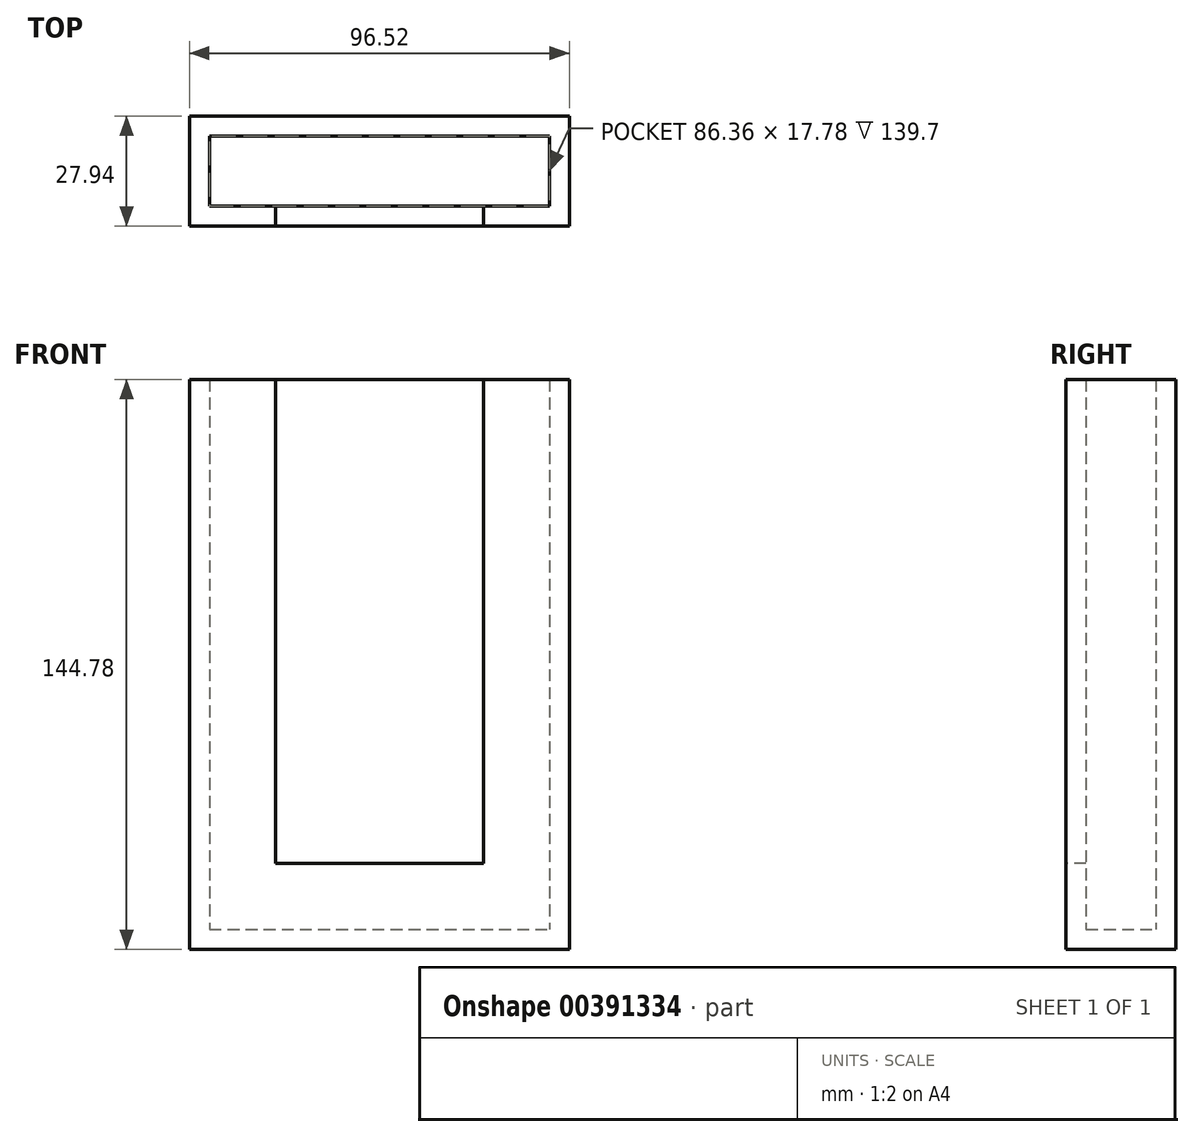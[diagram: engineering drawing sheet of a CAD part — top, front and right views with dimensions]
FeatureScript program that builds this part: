
annotation { "Feature Type Name" : "Feature", "Feature Type Description" : "" }
export const myFeature = defineFeature(function(context is Context, id is Id, definition is map)
    precondition{}
    {
        {
            var Q0;
            Q0=qCreatedBy(makeId("Front.planeOp"),FACE);
            var sketch = newSketch(context, id + "F0", { "sketchPlane" : qUnion([Q0])});
            skLineSegment(sketch, "E0.bottom", {"start": v(-60.88, 53.43) * mm, "end": v(35.64, 53.43) * mm});
            skLineSegment(sketch, "E0.top", {"start": v(-60.88, -91.35) * mm, "end": v(35.64, -91.35) * mm});
            skLineSegment(sketch, "E0.left", {"start": v(-60.88, 53.43) * mm, "end": v(-60.88, -91.35) * mm});
            skLineSegment(sketch, "E0.right", {"start": v(35.64, 53.43) * mm, "end": v(35.64, -91.35) * mm});
            skSolve(sketch);
        }
        {
            var Q0;
            Q0=makeQuery(id+"F0.imprint","IMPRINT",FACE,{"disambiguationData":[TD([[makeQuery(id+"F0.imprint","IMPRINT",EDGE,{"derivedFrom":sQuery(id+"F0.wireOp",EDGE,"E0.bottom")}),-1.0]])]});
            extrude(context, id + "F1", {"entities" : qUnion([Q0]), "depth" : 27.94 * mm});
        }
        {
            var Q0;
            Q0=makeQuery(id+"F1.opExtrude","SWEPT_FACE",FACE,{"disambiguationData":[OSD([sQuery(id+"F0.wireOp",EDGE,"E0.bottom")])]});
            shell(context, id + "F2", {"entities" : qUnion([Q0]), "thickness" : 5.08 * mm});
        }
        {
            var Q0;
            Q0=makeQuery(id+"F1.opExtrude","CAP_FACE",FACE,{"disambiguationData":[OSD([sQuery(id+"F0.wireOp",EDGE,"E0.bottom"),sQuery(id+"F0.wireOp",EDGE,"E0.top"),sQuery(id+"F0.wireOp",EDGE,"E0.left"),sQuery(id+"F0.wireOp",EDGE,"E0.right")])],"isStart":false});
            var sketch = newSketch(context, id + "F3", { "sketchPlane" : qUnion([Q0])});
            skLineSegment(sketch, "E1.0", {"start": v(-39.04, 74.08) * mm, "end": v(-39.04, -69.5) * mm});
            skLineSegment(sketch, "E1.2", {"start": v(13.8, -69.5) * mm, "end": v(13.8, 73.64) * mm});
            skLineSegment(sketch, "E1.3", {"start": v(-39.04, -69.5) * mm, "end": v(13.8, -69.5) * mm});
            skLineSegment(sketch, "E2", {"start": v(-39.04, 74.08) * mm, "end": v(13.8, 74.08) * mm});
            skSolve(sketch);
        }
        {
            var Q0;
            Q0=makeQuery(id+"F3.imprint","IMPRINT",FACE,{"disambiguationData":[TD([[makeQuery(id+"F3.imprint","IMPRINT",EDGE,{"derivedFrom":sQuery(id+"F3.wireOp",EDGE,"E1.0")}),1.0]])]});
            extrude(context, id + "F4", {"entities" : qUnion([Q0]), "operationType" : NewBodyOperationType.REMOVE, "oppositeDirection" : true, "depth" : 7.62 * mm});
        }
    });
